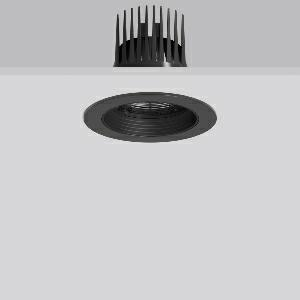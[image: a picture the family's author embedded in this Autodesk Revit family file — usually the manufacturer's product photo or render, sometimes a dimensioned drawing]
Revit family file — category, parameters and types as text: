
# Revit family: heledon_maxi_e_901761_003_76_3eb8
name_source: partatom
category: Lighting Fixtures
units: mm (PartAtom-declared; Revit-internal decimal feet)

## family parameters
Cut with Voids When Loaded = No
Host = Face
Light Source = No
Part Type = Normal
Room Calculation Point = No
Round Connector Dimension = Use Diameter
Shared = No

## types (1)
- HELEDON maxi E (1 x LED Modul 930, 2750 lm, 3000)
    Apparent Load = 25 VA
    Approval mark = CE
    CIE Flux Codes = 96 100 100 100 100
    Color Rendering = 90
    Color Temperature = 3000
    Default Elevation = 1800 mm
    Description = Series: HELEDON maxi
Round recessed downlight. Housing: die-cast aluminium, powder-coated. Black plastic ring and recessed LED to prevent glare from the side. Optical assembly with lens made of plastic (polycarbonate) for the best homogeneous light distribution - can be changed without tools. Best colour rendering index Ra>90. Suitable for Recessed ceiling mounting. Installation without tools thanks to spring fastening system. Including separate LED converter with connecting cable 600 mm.High quality converter without flickering and stroboscopic effect. Through-wiring box (5 pole) available as accessory. The following accessories can be mounted without use of tools: interchangeable lenses, decorative glasses, honeycomb louvre, clear and frosted diffusers, white interchangeable plastic ring. 
Colour: deep black, matt (RAL 9005)
Diameter: 162 mm
Height: 3 mm
Cut-out diameter: 152 mm
Recess height: 200 mm
Luminaire: recess height: 135 mm
Lamp: LED
Socket: without socket
Colour temperature: 3000K
Colour rendering index (CRI): 92
System power: 25 W
Rated luminous flux: 2750 lm
Luminous efficiency: 110 lm/W
Control gear: Converter, dimmable, DALI
Protection class: II
Type of protection: IP 20
    Height = 0 mm  [stored 0 ft]
    Lamp = 1 x LED Modul 930
    Lamp Light Flux = 2750 lm
    Lamp count = 1
    Length = 162 mm
    Lifetime = 50000 h
    Luminous efficacy = 110 lm/W
    Manufacturer = RZB
    ModVariant = No
    Model = 901761.003.76
    Mounting Place = Ceiling
    Mounting Type = Recessed
    Number of Poles = 1
    OnlyDefault = Yes
    Power Factor = 1
    Product Name = HELEDON maxi E
    Product group = Recessed downlights
    ProductGroupID = 402
    Protection Class = Protection class II
    Protection Degree = IP 20
    RLX_Detail_Level = 1
    RLX_Emergency_Light_Flux = 0 lm
    RLX_Emergency_Type = 0
    RLX_Emergency_Type_DB = No
    RlxData = <blob elided: 121677 chars, md5=86c2dc76>
    Socket = socket
    Standby Power = 0 W
    System Light Flux = 2750 lm
    System Power = 25 W
    Type Comments = Product without accessories
    Type Image = 901663.003.jpg
    URL = http://relux.com
    VarID = ---
    Voltage = 230 V
    Voltage Range = 220-240 V
    Weight = 0.00 kg
    Width = 0 mm  [stored 0 ft]

note: [stored X ft] marks values corroborated as IEEE doubles in the binary element streams (Revit-internal decimal feet)

## geometry (parser evidence)
native form markers: Blend x4, Sweep x10
no freeform markers — native parametric forms only
